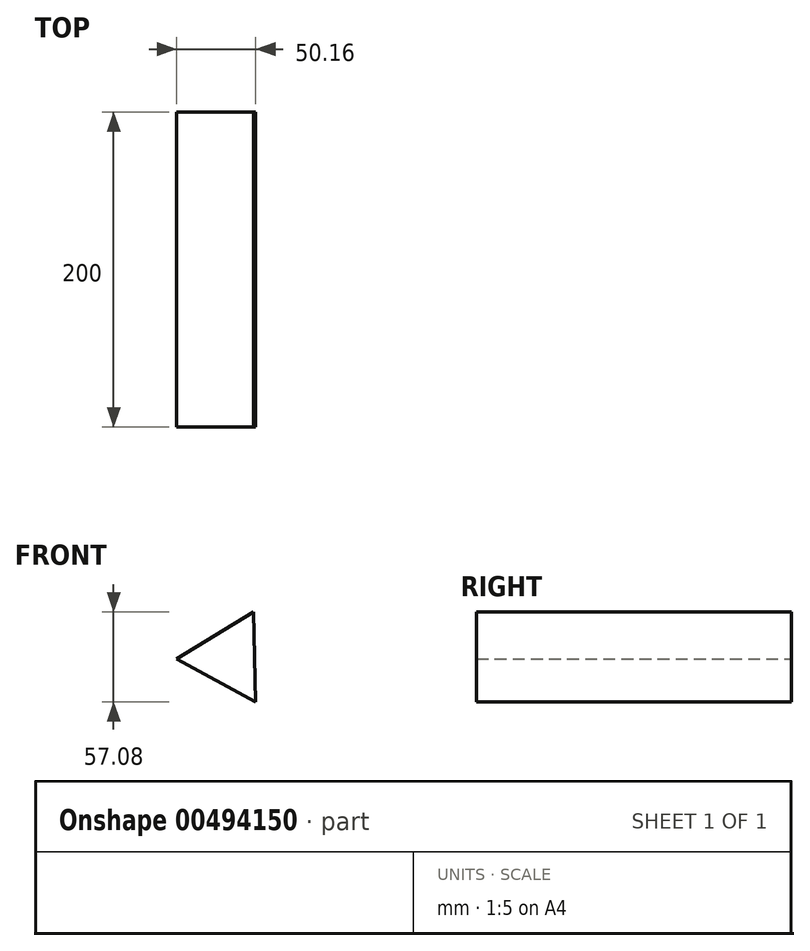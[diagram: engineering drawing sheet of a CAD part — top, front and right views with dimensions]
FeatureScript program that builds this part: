
annotation { "Feature Type Name" : "Feature", "Feature Type Description" : "" }
export const myFeature = defineFeature(function(context is Context, id is Id, definition is map)
    precondition{}
    {
        {
            var Q0;
            Q0=qCreatedBy(makeId("Front.planeOp"),FACE);
            var sketch = newSketch(context, id + "F0", { "sketchPlane" : qUnion([Q0])});
            skCircle(sketch, "E0.cCircle", {"center": v(0, 5.3) * mm, "radius": 32.97 * mm, "construction": true});
            skLineSegment(sketch, "E0.0", {"start": v(17.21, -22.8) * mm, "end": v(-32.95, 4.46) * mm});
            skLineSegment(sketch, "E0.1", {"start": v(-32.95, 4.46) * mm, "end": v(15.74, 34.27) * mm});
            skLineSegment(sketch, "E0.2", {"start": v(15.74, 34.27) * mm, "end": v(17.21, -22.8) * mm});
            skSolve(sketch);
        }
        {
            var Q0;
            Q0=makeQuery(id+"F0.imprint","IMPRINT",FACE,{"disambiguationData":[TD([[makeQuery(id+"F0.imprint","IMPRINT",EDGE,{"derivedFrom":sQuery(id+"F0.wireOp",EDGE,"E0.0")}),-1.0]])]});
            extrude(context, id + "F1", {"entities" : qUnion([Q0]), "depth" : 200 * mm});
        }
    });
